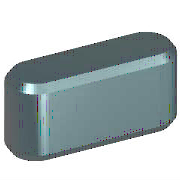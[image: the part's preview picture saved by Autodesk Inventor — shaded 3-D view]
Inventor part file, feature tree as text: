
AUTODESK INVENTOR PART (.ipt)
format: ipt  version: 2025 (Build 290162000, 162)  size: 139,776 bytes
history: native  units: mm (DEFAULTED — no unit token found)
features: plane x3, extrude x1
ambient origin geometry x8: Origin, YZ Plane, XZ Plane, XY Plane, X Axis, Y Axis, Z Axis, Center Point
bodies: Solid1 (feature_tree)
feature tree (4):
  plane  "Work Plane1"
  plane  "Work Plane2"
  extrude  "轴承体1"  Depth=7.0mm
  plane  "Work Plane3"
